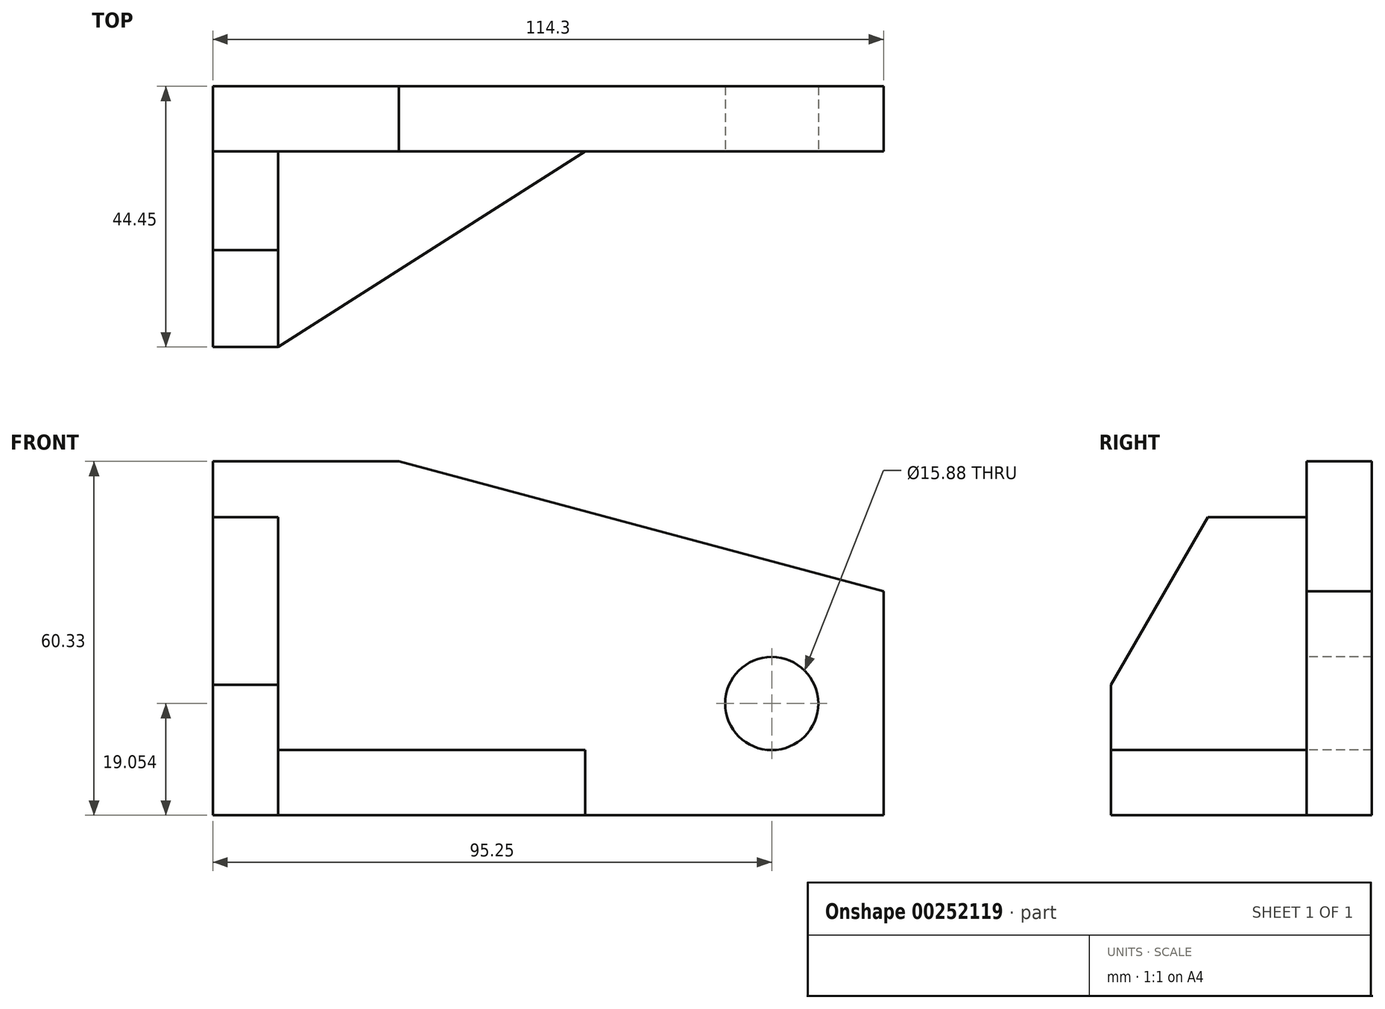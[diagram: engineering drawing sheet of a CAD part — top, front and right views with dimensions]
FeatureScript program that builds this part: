
annotation { "Feature Type Name" : "Feature", "Feature Type Description" : "" }
export const myFeature = defineFeature(function(context is Context, id is Id, definition is map)
    precondition{}
    {
        {
            var Q0;
            Q0=qCreatedBy(makeId("Front.planeOp"),FACE);
            var sketch = newSketch(context, id + "F0", { "sketchPlane" : qUnion([Q0])});
            skLineSegment(sketch, "E0", {"start": v(-95.15, 36.48) * mm, "end": v(-95.15, -23.85) * mm});
            skLineSegment(sketch, "E1", {"start": v(-95.15, 36.48) * mm, "end": v(-63.4, 36.48) * mm});
            skLineSegment(sketch, "E2", {"start": v(-95.15, -23.85) * mm, "end": v(19.15, -23.85) * mm});
            skLineSegment(sketch, "E3", {"start": v(-63.4, 36.48) * mm, "end": v(19.15, 14.36) * mm});
            skLineSegment(sketch, "E4", {"start": v(19.15, 14.36) * mm, "end": v(19.15, -23.85) * mm});
            skSolve(sketch);
        }
        {
            var Q0;
            Q0=makeQuery(id+"F0.imprint","IMPRINT",FACE,{"disambiguationData":[TD([[makeQuery(id+"F0.imprint","IMPRINT",EDGE,{"derivedFrom":sQuery(id+"F0.wireOp",EDGE,"E0")}),1.0]])]});
            extrude(context, id + "F1", {"entities" : qUnion([Q0]), "depth" : 11.1 * mm});
        }
        {
            var Q0;
            Q0=makeQuery(id+"F1.opExtrude","CAP_FACE",FACE,{"disambiguationData":[OSD([sQuery(id+"F0.wireOp",EDGE,"E0"),sQuery(id+"F0.wireOp",EDGE,"E1"),sQuery(id+"F0.wireOp",EDGE,"E2"),sQuery(id+"F0.wireOp",EDGE,"E3"),sQuery(id+"F0.wireOp",EDGE,"E4")])],"isStart":false});
            var sketch = newSketch(context, id + "F2", { "sketchPlane" : qUnion([Q0])});
            skCircle(sketch, "E5", {"center": v(0.1, -4.8) * mm, "radius": 7.94 * mm});
            skSolve(sketch);
        }
        {
            var Q0;
            Q0=makeQuery(id+"F2.imprint","IMPRINT",FACE,{"disambiguationData":[TD([[makeQuery(id+"F2.imprint","IMPRINT",EDGE,{"derivedFrom":sQuery(id+"F2.wireOp",EDGE,"E5")}),1.0]])]});
            extrude(context, id + "F3", {"entities" : qUnion([Q0]), "operationType" : NewBodyOperationType.REMOVE, "oppositeDirection" : true, "depth" : 25.4 * mm});
        }
        {
            var Q0;
            Q0=makeQuery(id+"F1.opExtrude","SWEPT_FACE",FACE,{"disambiguationData":[OSD([sQuery(id+"F0.wireOp",EDGE,"E2")])]});
            var sketch = newSketch(context, id + "F4", { "sketchPlane" : qUnion([Q0])});
            skLineSegment(sketch, "E6", {"start": v(-84.04, 44.45) * mm, "end": v(-84.04, -4.3) * mm});
            skLineSegment(sketch, "E7", {"start": v(-84.04, 44.45) * mm, "end": v(-31.65, 11.11) * mm});
            skSolve(sketch);
        }
        {
            var Q0;
            {var subQ0=sQuery(id+"F4.wireOp",EDGE,"E7");Q0=makeQuery(id+"F4.imprint","IMPRINT",FACE,{"disambiguationData":[TD([[makeQuery(id+"F4.imprint","IMPRINT",EDGE,{"derivedFrom":subQ0}),-1.0]])]});}
            extrude(context, id + "F5", {"entities" : qUnion([Q0]), "operationType" : NewBodyOperationType.ADD, "oppositeDirection" : true, "depth" : 11.1 * mm});
        }
        {
            var Q0;
            Q0=makeQuery(id+"F5.opExtrude","SWEPT_FACE",FACE,{"disambiguationData":[OSD([sQuery(id+"F4.wireOp",EDGE,"E6")])]});
            var sketch = newSketch(context, id + "F6", { "sketchPlane" : qUnion([Q0])});
            skLineSegment(sketch, "E8", {"start": v(44.45, -23.85) * mm, "end": v(44.45, -1.62) * mm});
            skLineSegment(sketch, "E9", {"start": v(11.11, -23.85) * mm, "end": v(11.11, 26.95) * mm});
            skPoint(sketch, "E9.endSnap0", {"position": v(11.11, -18.29) * mm});
            skLineSegment(sketch, "E10", {"start": v(44.45, -1.62) * mm, "end": v(27.95, 26.95) * mm});
            skLineSegment(sketch, "E11", {"start": v(11.11, 26.95) * mm, "end": v(27.95, 26.95) * mm});
            skSolve(sketch);
        }
        {
            var Q0;
            {var subQ1=sQuery(id+"F4.wireOp",EDGE,"E6");var subQ2=makeQuery(id+"F5.opExtrude","CAP_EDGE",EDGE,{"disambiguationData":[OSD([subQ1])],"isStart":true});Q0=makeQuery(id+"F6.imprint","IMPRINT",FACE,{"disambiguationData":[TD([[makeQuery(id+"F6.imprint","IMPRINT",EDGE,{"derivedFrom":subQ2}),-1.0]])]});}
            var Q1;
            {var subQ0=sQuery(id+"F6.wireOp",EDGE,"E10");Q1=makeQuery(id+"F6.imprint","IMPRINT",FACE,{"disambiguationData":[TD([[makeQuery(id+"F6.imprint","IMPRINT",EDGE,{"derivedFrom":subQ0}),1.0]])]});}
            extrude(context, id + "F7", {"entities" : qUnion([Q0, Q1]), "operationType" : NewBodyOperationType.ADD, "depth" : 11.1 * mm});
        }
    });
